# Revit family: 57_CRD_ME_Care_H1C
name_source: partatom
category: Mechanical Equipment
units: mm (PartAtom-declared; Revit-internal decimal feet)

## family parameters
Always vertical = Yes
Classification = None
Cut with Voids When Loaded = Yes
Part Type = Normal
Room Calculation Point = Yes
Round Connector Dimension = Use Diameter
Shared = No
Work Plane-Based = Yes

## types (1)
- 1320  x 485 x 142
    Default Elevation = 1219 mm
    Description = ClimaRad Sensa H2X ventilatie-unit
    Manufacturer = ClimaRad
    Model = Sensa H2X
    borstwering = 705 mm  [stored 2.31299 ft]
    diameter_hydronic_return = 13 mm  [stored 0.0426509 ft]
    diameter_hydronic_supply = 13 mm  [stored 0.0426509 ft]
    diepte = 160 mm  [stored 0.524934 ft]
    hart_doorvoer_tov_ok_kast = 366 mm
    hart_wcd_tov_vloerpeil = 217 mm  [stored 0.711942 ft]
    hoh_ventilatie_doorvoeren = 1098 mm  [stored 3.60236 ft]
    hoogte = 655 mm  [stored 2.14895 ft]
    hydronic_return_flow = 0.0 L/s
    hydronic_supply_flow = 0.0 L/s
    kader_bovenkant = 8 mm  [stored 0.0262467 ft]
    lengte = 1530 mm  [stored 5.01969 ft]
    positie_wcd_uit_hart_unit = 677 mm  [stored 2.22113 ft]
    rooster_offset_X_links_vrij_invullen = 0 mm  [stored 0 ft]
    ruimte_onder_unit = 50 mm  [stored 0.164042 ft]
    schacht = Yes
    voltage = 230 V

note: [stored X ft] marks values corroborated as IEEE doubles in the binary element streams (Revit-internal decimal feet)

## geometry (parser evidence)
native form markers: Sweep x11
no freeform markers — native parametric forms only
